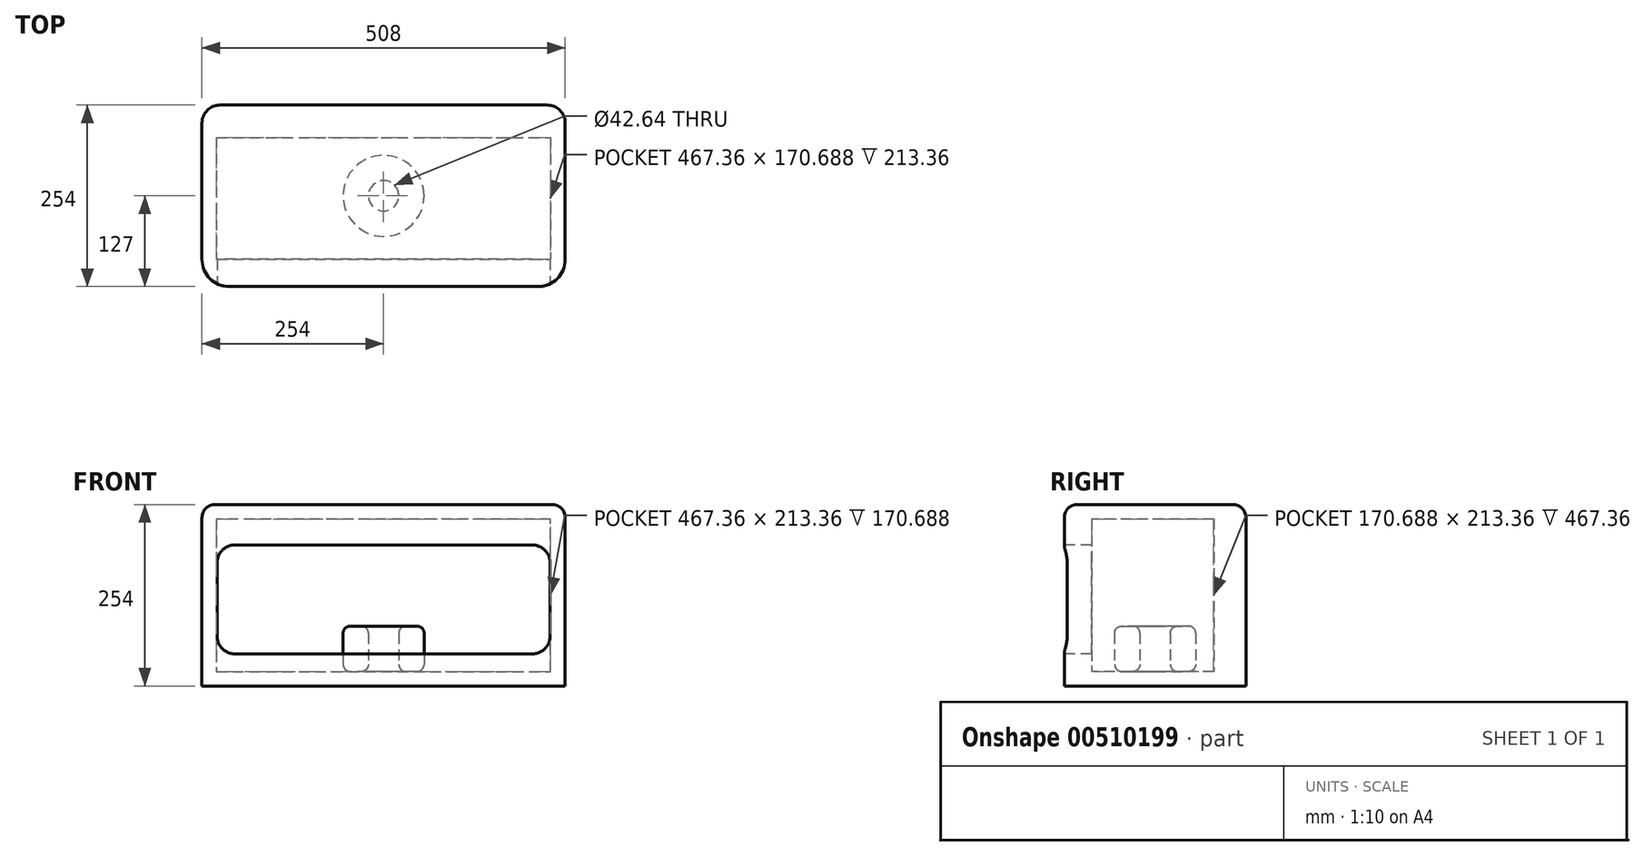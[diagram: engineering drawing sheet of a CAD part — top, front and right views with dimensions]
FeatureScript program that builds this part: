
annotation { "Feature Type Name" : "Feature", "Feature Type Description" : "" }
export const myFeature = defineFeature(function(context is Context, id is Id, definition is map)
    precondition{}
    {
        {
            var Q0;
            Q0=qCreatedBy(makeId("Top.planeOp"),FACE);
            var sketch = newSketch(context, id + "F0", { "sketchPlane" : qUnion([Q0])});
            skLineSegment(sketch, "E0.bottom", {"start": v(215.9, -127) * mm, "end": v(-215.9, -127) * mm});
            skLineSegment(sketch, "E0.top", {"start": v(228.6, 127) * mm, "end": v(-228.6, 127) * mm});
            skLineSegment(sketch, "E0.left", {"start": v(254, -88.9) * mm, "end": v(254, 101.6) * mm});
            skLineSegment(sketch, "E0.right", {"start": v(-254, -88.9) * mm, "end": v(-254, 101.6) * mm});
            skPoint(sketch, "E0.middle", {"position": v(0, 0) * mm});
            skPoint(sketch, "E1.visualSharp", {"position": v(-254, -127) * mm});
            skArc(sketch, "E1.filletArc", {"start": v(-254, -88.9) * mm, "mid": v(-242.84, -115.84) * mm, "end": v(-215.9, -127) * mm});
            skPoint(sketch, "E2.visualSharp", {"position": v(254, -127) * mm});
            skArc(sketch, "E2.filletArc", {"start": v(215.9, -127) * mm, "mid": v(242.84, -115.84) * mm, "end": v(254, -88.9) * mm});
            skPoint(sketch, "E3.visualSharp", {"position": v(254, 127) * mm});
            skArc(sketch, "E3.filletArc", {"start": v(254, 101.6) * mm, "mid": v(246.56, 119.56) * mm, "end": v(228.6, 127) * mm});
            skPoint(sketch, "E4.visualSharp", {"position": v(-254, 127) * mm});
            skArc(sketch, "E4.filletArc", {"start": v(-228.6, 127) * mm, "mid": v(-246.56, 119.56) * mm, "end": v(-254, 101.6) * mm});
            skLineSegment(sketch, "E5", {"start": v(-254, -88.9) * mm, "end": v(254, -88.9) * mm});
            skSolve(sketch);
        }
        {
            var Q0;
            Q0=makeQuery(id+"F0.imprint","IMPRINT",FACE,{"disambiguationData":[TD([[makeQuery(id+"F0.imprint","IMPRINT",EDGE,{"derivedFrom":sQuery(id+"F0.wireOp",EDGE,"E0.bottom")}),-1.0]])]});
            extrude(context, id + "F1", {"entities" : qUnion([Q0]), "depth" : 254 * mm});
        }
        {
            var Q0;
            Q0=makeQuery(id+"F0.imprint","IMPRINT",FACE,{"disambiguationData":[TD([[makeQuery(id+"F0.imprint","IMPRINT",EDGE,{"derivedFrom":sQuery(id+"F0.wireOp",EDGE,"E0.top")}),1.0]])]});
            extrude(context, id + "F2", {"entities" : qUnion([Q0]), "depth" : 254 * mm});
        }
        {
            var Q0;
            Q0=makeQuery(id+"F2.opExtrude","SWEPT_FACE",FACE,{"disambiguationData":[OSD([sQuery(id+"F0.wireOp",EDGE,"E5")])]});
            var sketch = newSketch(context, id + "F3", { "sketchPlane" : qUnion([Q0])});
            skLineSegment(sketch, "E6.0", {"start": v(-233.68, 20.32) * mm, "end": v(233.68, 20.32) * mm});
            skLineSegment(sketch, "E6.1", {"start": v(-233.68, 233.68) * mm, "end": v(-233.68, 20.32) * mm});
            skLineSegment(sketch, "E6.2", {"start": v(233.68, 233.68) * mm, "end": v(-233.68, 233.68) * mm});
            skLineSegment(sketch, "E6.3", {"start": v(233.68, 20.32) * mm, "end": v(233.68, 233.68) * mm});
            skSolve(sketch);
        }
        {
            var Q0;
            Q0=makeQuery(id+"F3.imprint","IMPRINT",FACE,{"disambiguationData":[TD([[makeQuery(id+"F3.imprint","IMPRINT",EDGE,{"derivedFrom":sQuery(id+"F3.wireOp",EDGE,"E6.0")}),1.0]])]});
            extrude(context, id + "F4", {"entities" : qUnion([Q0]), "operationType" : NewBodyOperationType.ADD, "oppositeDirection" : true, "depth" : 170.18 * mm});
        }
        {
            var Q0;
            Q0=makeQuery(id+"F3.imprint","IMPRINT",FACE,{"disambiguationData":[TD([[makeQuery(id+"F3.imprint","IMPRINT",EDGE,{"derivedFrom":sQuery(id+"F3.wireOp",EDGE,"E6.0")}),1.0]])]});
            extrude(context, id + "F5", {"entities" : qUnion([Q0]), "operationType" : NewBodyOperationType.REMOVE, "oppositeDirection" : true, "depth" : 170.7 * mm});
        }
        {
            var Q0;
            Q0=makeQuery(id+"F5.boolean.opBoolean","COPY",FACE,{"derivedFrom":makeQuery(id+"F5.opExtrude","SWEPT_FACE",FACE,{"disambiguationData":[OSD([sQuery(id+"F3.wireOp",EDGE,"E6.0")])]})});
            var sketch = newSketch(context, id + "F6", { "sketchPlane" : qUnion([Q0])});
            skCircle(sketch, "E7", {"center": v(0, 0) * mm, "radius": 56.65 * mm});
            skCircle(sketch, "E8", {"center": v(0, 0) * mm, "radius": 21.32 * mm});
            skSolve(sketch);
        }
        {
            var Q0;
            Q0=makeQuery(id+"F6.imprint","IMPRINT",FACE,{"disambiguationData":[TD([[makeQuery(id+"F6.imprint","IMPRINT",EDGE,{"derivedFrom":sQuery(id+"F6.wireOp",EDGE,"E7")}),1.0]])]});
            extrude(context, id + "F7", {"entities" : qUnion([Q0]), "depth" : 63.5 * mm});
        }
        {
            var Q0;
            Q0=makeQuery(id+"F7.opExtrude","CAP_EDGE",EDGE,{"disambiguationData":[OSD([sQuery(id+"F6.wireOp",EDGE,"E7")])],"isStart":false});
            var Q1;
            Q1=makeQuery(id+"F7.opExtrude","CAP_EDGE",EDGE,{"disambiguationData":[OSD([sQuery(id+"F6.wireOp",EDGE,"E8")])],"isStart":false});
            var Q2;
            Q2=makeQuery(id+"F7.opExtrude","SWEPT_FACE",FACE,{"disambiguationData":[OSD([sQuery(id+"F6.wireOp",EDGE,"E8")])]});
            var Q3;
            Q3=makeQuery(id+"F7.opExtrude","CAP_EDGE",EDGE,{"disambiguationData":[OSD([sQuery(id+"F6.wireOp",EDGE,"E7")])],"isStart":true});
            fillet(context, id + "F8", {"entities" : qUnion([Q0, Q1, Q2, Q3]), "radius" : 9.8 * mm, "tangentPropagation" : true, "allowEdgeOverflow" : false});
        }
        {
            var Q0;
            Q0=makeQuery(id+"F1.opExtrude","SWEPT_FACE",FACE,{"disambiguationData":[OSD([sQuery(id+"F0.wireOp",EDGE,"E0.bottom")])]});
            var sketch = newSketch(context, id + "F9", { "sketchPlane" : qUnion([Q0])});
            skLineSegment(sketch, "E9.bottom", {"start": v(207.56, 44.88) * mm, "end": v(-207.56, 44.88) * mm});
            skLineSegment(sketch, "E9.top", {"start": v(207.56, 197.59) * mm, "end": v(-207.56, 197.59) * mm});
            skLineSegment(sketch, "E9.left", {"start": v(232.96, 70.28) * mm, "end": v(232.96, 172.19) * mm});
            skLineSegment(sketch, "E9.right", {"start": v(-232.96, 70.28) * mm, "end": v(-232.96, 172.19) * mm});
            skPoint(sketch, "E9.middle", {"position": v(0, 121.23) * mm});
            skPoint(sketch, "E10.visualSharp", {"position": v(232.96, 197.59) * mm});
            skArc(sketch, "E10.filletArc", {"start": v(232.96, 172.19) * mm, "mid": v(225.52, 190.15) * mm, "end": v(207.56, 197.59) * mm});
            skPoint(sketch, "E11.visualSharp", {"position": v(-232.96, 197.59) * mm});
            skArc(sketch, "E11.filletArc", {"start": v(-207.56, 197.59) * mm, "mid": v(-225.52, 190.15) * mm, "end": v(-232.96, 172.19) * mm});
            skPoint(sketch, "E12.visualSharp", {"position": v(-232.96, 44.88) * mm});
            skArc(sketch, "E12.filletArc", {"start": v(-232.96, 70.28) * mm, "mid": v(-225.52, 52.32) * mm, "end": v(-207.56, 44.88) * mm});
            skPoint(sketch, "E13.visualSharp", {"position": v(232.96, 44.88) * mm});
            skArc(sketch, "E13.filletArc", {"start": v(207.56, 44.88) * mm, "mid": v(225.52, 52.32) * mm, "end": v(232.96, 70.28) * mm});
            skSolve(sketch);
        }
        {
            var Q0;
            {var subQ10=sQuery(id+"F9.wireOp",EDGE,"E9.bottom");Q0=makeQuery(id+"F9.imprint","IMPRINT",FACE,{"disambiguationData":[TD([[makeQuery(id+"F9.imprint","IMPRINT",EDGE,{"derivedFrom":subQ10}),-1.0]])]});}
            var Q1;
            {var subQ0=sQuery(id+"F9.wireOp",EDGE,"E9.left");Q1=makeQuery(id+"F9.imprint","IMPRINT",FACE,{"disambiguationData":[TD([[makeQuery(id+"F9.imprint","IMPRINT",EDGE,{"derivedFrom":subQ0}),1.0]])]});}
            var Q2;
            {var subQ0=sQuery(id+"F9.wireOp",EDGE,"E9.right");Q2=makeQuery(id+"F9.imprint","IMPRINT",FACE,{"disambiguationData":[TD([[makeQuery(id+"F9.imprint","IMPRINT",EDGE,{"derivedFrom":subQ0}),-1.0]])]});}
            extrude(context, id + "F10", {"entities" : qUnion([Q0, Q1, Q2]), "operationType" : NewBodyOperationType.REMOVE, "oppositeDirection" : true, "depth" : 50.8 * mm});
        }
        {
            var Q0;
            Q0=makeQuery(id+"F1.opExtrude","CAP_EDGE",EDGE,{"disambiguationData":[OSD([sQuery(id+"F0.wireOp",EDGE,"E2.filletArc")])],"isStart":false});
            var Q1;
            Q1=makeQuery(id+"F2.opExtrude","CAP_EDGE",EDGE,{"disambiguationData":[OSD([sQuery(id+"F0.wireOp",EDGE,"E0.left")])],"isStart":false});
            var Q2;
            Q2=makeQuery(id+"F2.opExtrude","CAP_EDGE",EDGE,{"disambiguationData":[OSD([sQuery(id+"F0.wireOp",EDGE,"E3.filletArc")])],"isStart":false});
            var Q3;
            Q3=makeQuery(id+"F2.opExtrude","CAP_EDGE",EDGE,{"disambiguationData":[OSD([sQuery(id+"F0.wireOp",EDGE,"E0.top")])],"isStart":false});
            var Q4;
            Q4=makeQuery(id+"F2.opExtrude","CAP_EDGE",EDGE,{"disambiguationData":[OSD([sQuery(id+"F0.wireOp",EDGE,"E4.filletArc")])],"isStart":false});
            var Q5;
            Q5=makeQuery(id+"F2.opExtrude","CAP_EDGE",EDGE,{"disambiguationData":[OSD([sQuery(id+"F0.wireOp",EDGE,"E0.right")])],"isStart":false});
            var Q6;
            Q6=makeQuery(id+"F1.opExtrude","CAP_EDGE",EDGE,{"disambiguationData":[OSD([sQuery(id+"F0.wireOp",EDGE,"E1.filletArc")])],"isStart":false});
            var Q7;
            Q7=makeQuery(id+"F1.opExtrude","CAP_EDGE",EDGE,{"disambiguationData":[OSD([sQuery(id+"F0.wireOp",EDGE,"E0.bottom")])],"isStart":false});
            fillet(context, id + "F11", {"entities" : qUnion([Q0, Q1, Q2, Q3, Q4, Q5, Q6, Q7]), "radius" : 18.4 * mm, "tangentPropagation" : true, "allowEdgeOverflow" : false});
        }
    });
